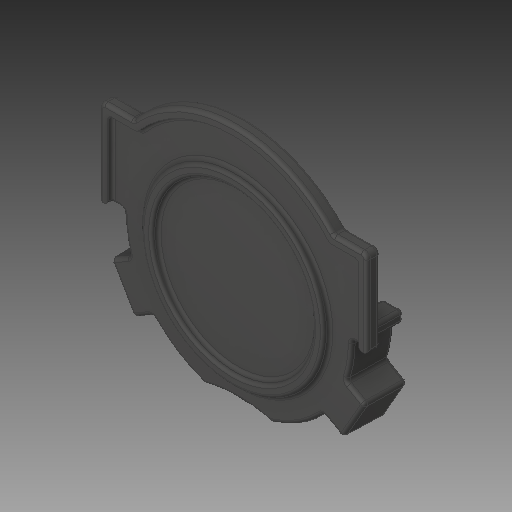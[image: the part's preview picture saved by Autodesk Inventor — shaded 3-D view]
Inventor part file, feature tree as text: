
AUTODESK INVENTOR PART (.ipt)
format: ipt  version: 2017 (Build 210142000, 142)  size: 862,720 bytes
history: native  units: in
note: dims shown in document units (in); Inventor stores cm internally (conversion verified against a paired STEP export)
features: fillet x1
ambient origin geometry x8: Origin, YZ Plane, XZ Plane, XY Plane, X Axis, Y Axis, Z Axis, Center Point
bodies: Solid1 (feature_tree)
feature tree (1):
  fillet  "Fillet13"  [1 undecoded]
note: 1 required parameter value undecoded (feature->parameter linkage not recoverable at this tier; creation-order binding heuristic only, values carry confidence <= 0.55)
